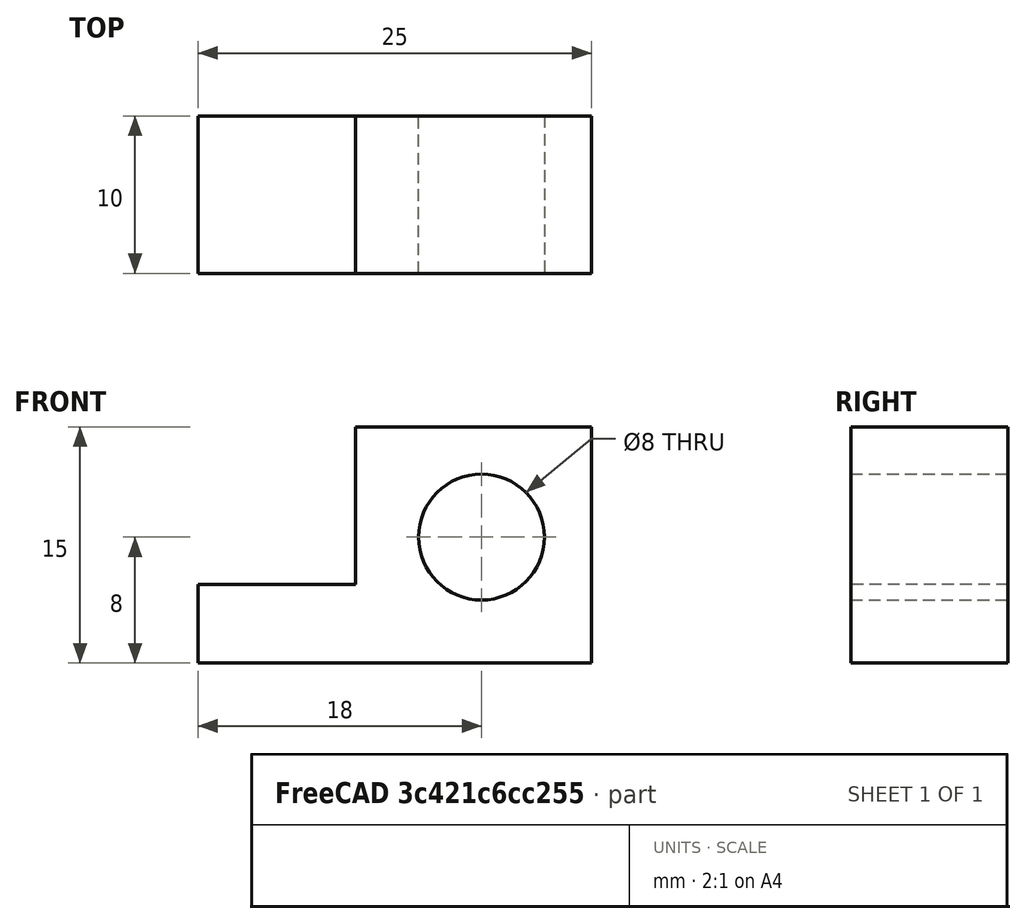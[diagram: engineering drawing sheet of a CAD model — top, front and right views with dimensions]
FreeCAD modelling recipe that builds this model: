
FCSTD DOCUMENT  (FreeCAD 1.0R39109 (Git))
Label: 02
License: All rights reserved
LicenseURL: https://en.wikipedia.org/wiki/All_rights_reserved
objects: Sketcher::SketchObject×1, PartDesign::Pad×1, PartDesign::Body×1
note: 6 computed .brp shape members not serialized (recipe doc carries the construction recipe); baked Part::Feature solids carry a one-line shape summary decoded from their .brp

FEATURE [Sketcher::SketchObject] Sketch
  ArcFitTolerance = 1e-06
  AttachmentSupport = -> [XZ_Plane]
  FullyConstrained = true
  MakeInternals = false
  MapMode = 5
  Placement = pos=(0,0,0) rot=(1,0,0;1.5708rad)
  sketch-geometry (7):
    g0: LineSegment StartX=0 StartY=0 StartZ=0 EndX=0 EndY=15 EndZ=0
    g1: LineSegment StartX=0 StartY=15 StartZ=0 EndX=-15 EndY=15 EndZ=0
    g2: LineSegment StartX=-15 StartY=15 StartZ=0 EndX=-15 EndY=5 EndZ=0
    g3: LineSegment StartX=-15 StartY=5 StartZ=0 EndX=-25 EndY=5 EndZ=0
    g4: LineSegment StartX=-25 StartY=5 StartZ=0 EndX=-25 EndY=0 EndZ=0
    g5: LineSegment StartX=-25 StartY=0 StartZ=0 EndX=0 EndY=0 EndZ=0
    g6: Circle CenterX=-7 CenterY=8 CenterZ=0 NormalX=0 NormalY=0 NormalZ=1 AngleXU=0 Radius=4
  constraints (21):
    c: Coincident(g0,g-1)
    c: PointOnObject(g0,g-2)
    c: Coincident(g1,g0)
    c: Horizontal(g1)
    c: Coincident(g1,g2)
    c: Vertical(g2)
    c: Coincident(g2,g3)
    c: Coincident(g3,g4)
    c: Vertical(g4)
    c: Coincident(g5,g4)
    c: Coincident(g5,g0)
    c: Horizontal(g5)
    c: DistanceX(g5,g5) = 25
    c: DistanceX(g1,g1) = 15
    c: DistanceX(g3,g3) = 10
    c: DistanceY(g2,g2) = 10
    c: DistanceY(g0,g0) = 15
    c: DistanceY(g4,g4) = 5
    c: Diameter(g6) = 8
    c: DistanceX(g6,g0) = 7
    c: DistanceY(g0,g6) = 8
FEATURE [PartDesign::Pad] Pad
  Direction = (0,-1,2e-16)
  Length = 10
  Length2 = 10
  Midplane = true
  Placement = pos=(0,0,0) rot=(1,0,0;1.5708rad)
  Profile = -> Sketch
  ReferenceAxis = -> Sketch [N_Axis]
  Refine = true
  Suppressed = false
  Type = 0
FEATURE [PartDesign::Body] Body
  AllowCompound = false
  Group = -> [Sketch,Pad]
  Origin = -> Origin
  Tip = -> Pad
